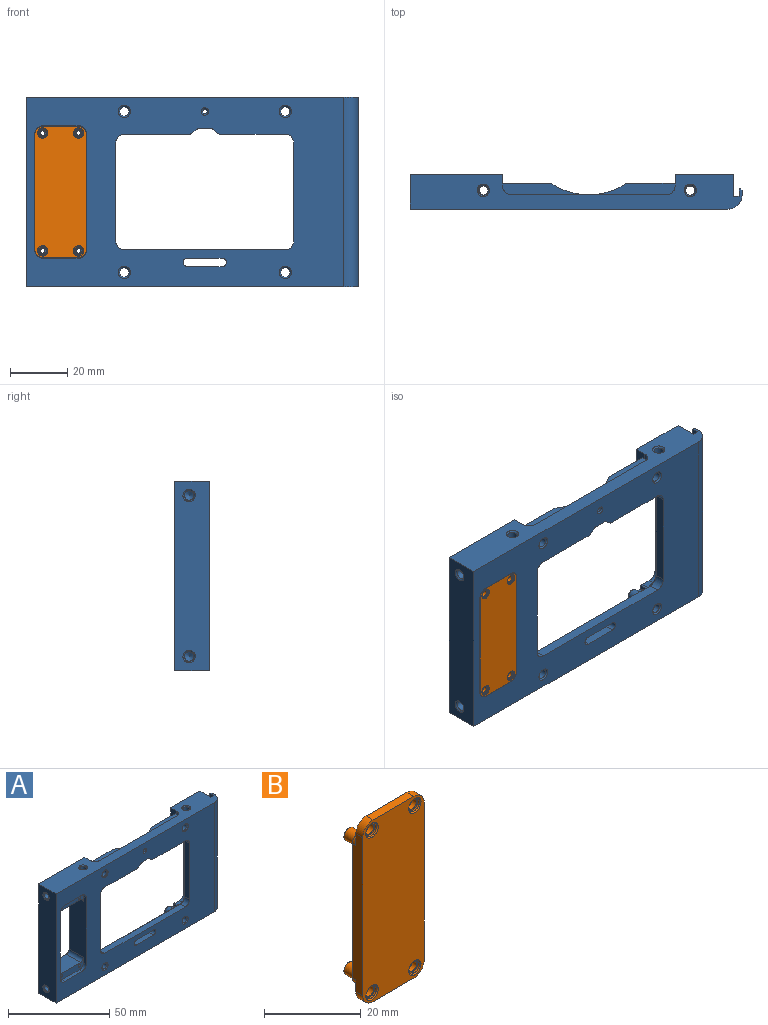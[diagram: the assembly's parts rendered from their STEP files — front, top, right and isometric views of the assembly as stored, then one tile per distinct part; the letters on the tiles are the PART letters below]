
ASSEMBLY  parts=2 mates=1
PART A: 193 faces, bbox 115.5x12x66 mm
  f0: plane 110.5x66mm, normal (0,-1,0), area 3867.2mm2, adj f15,f33,f34,f35,f36,f37,f38,f39
  f1: cylinder r=2mm len=10mm, axis (0,1,0), area 31.4mm2, adj f2,f31,f121,f173
  f2: plane 14.1x10mm, normal (0,0,-1), area 141mm2, adj f1,f3,f31,f173
  f3: cylinder r=2mm len=10mm, axis (0,1,0), area 31.4mm2, adj f2,f31,f122,f173
  f4: cylinder r=2mm len=10mm, axis (0,1,0), area 31.4mm2, adj f5,f31,f122,f177
  f5: plane 14.1x10mm, normal (0,0,1), area 141mm2, adj f4,f6,f31,f177
  f6: cylinder r=2mm len=10mm, axis (0,1,0), area 31.4mm2, adj f5,f31,f121,f177
  f7: cylinder r=0.8mm len=10mm, axis (0,-1,0), area 50.3mm2, adj f31,f173
  f8: cylinder r=0.8mm len=10mm, axis (0,-1,0), area 50.3mm2, adj f31,f177
  f9: cylinder r=0.8mm len=10mm, axis (0,-1,0), area 50.3mm2, adj f31,f177
  f10: cylinder r=0.8mm len=10mm, axis (0,-1,0), area 50.3mm2, adj f31,f173
  f11: plane 4.5x4.26mm, normal (1,0,0), area 19.2mm2, adj f15,f21,f139,f148
  f12: plane 4.5x4.26mm, normal (-1,0,0), area 19.2mm2, adj f15,f21,f140,f149
  f13: cylinder r=3.5mm len=4.5mm, axis (0,-1,0), area 6.6mm2, adj f21,f113,f139,f147
  f14: cylinder r=3.5mm len=4.5mm, axis (0,-1,0), area 6.6mm2, adj f18,f21,f140,f150
  f15: plane 115.5x12mm, normal (0,0,-1), area 923.5mm2, adj f0,f11,f12,f21,f24,f31,f54,f56
  f16: cylinder r=1.65mm len=8.5mm, axis (0,1,0), area 88.1mm2, adj f123,f140
  f17: cylinder r=1.65mm len=8.5mm, axis (0,1,0), area 88.1mm2, adj f126,f139
  f18: cylinder r=5mm len=7.5mm, axis (0,-1,0), area 16mm2, adj f14,f21,f24,f90,f119,f140
  f19: cylinder r=2mm len=4.5mm, axis (0,-1,0), area 26.3mm2, adj f21,f140,f149,f150
  f20: cylinder r=2mm len=4.5mm, axis (0,-1,0), area 26.3mm2, adj f21,f139,f147,f148
  f21: plane 78x56.5mm, normal (0,1,0), area 1353.3mm2, adj f11,f12,f13,f14,f15,f18,f19,f20
  f22: plane 8.11x7.5mm, normal (0,0,-1), area 48mm2, adj f21,f24,f49,f94,f116,f128,f138
  f23: plane 8.11x7.5mm, normal (0,0,-1), area 52.5mm2, adj f21,f31,f69,f93,f117,f127,f135
  f24: plane 66x20.3mm, normal (0,1,0), area 508.5mm2, adj f15,f18,f22,f55,f59,f86,f87,f90
  f25: cylinder r=24mm len=26.53mm, axis (0,0,1), area 208.8mm2, adj f28,f29,f30,f57,f127,f128
  f26: cylinder r=1.65mm len=8.5mm, axis (0,1,0), area 88.1mm2, adj f125,f127
  f27: cylinder r=1.65mm len=8.5mm, axis (0,1,0), area 88.1mm2, adj f124,f128
  f28: plane 43.29x4.5mm, normal (0,0,-1), area 122.8mm2, adj f21,f25,f127,f128,f136,f137
  f29: plane 30x4mm, normal (0,0,1), area 82.1mm2, adj f25,f114,f115,f116,f128
  f30: plane 30x4mm, normal (0,0,1), area 82.1mm2, adj f25,f114,f117,f118,f127
  f31: plane 66x32.2mm, normal (0,1,0), area 956.1mm2, adj f1,f2,f3,f4,f5,f6,f7,f8
  f32: plane 7.5x3.18mm, normal (0,0,1), area 21.8mm2, adj f21,f31,f64,f91,f113
  f33: plane 56.05x3.5mm, normal (0,0,1), area 196.2mm2, adj f0,f46,f47,f105
  f34: cylinder r=3mm len=3.5mm, axis (0,1,0), area 16.5mm2, adj f0,f35,f48,f111
  f35: plane 22.53x3.5mm, normal (0,0,-1), area 78.8mm2, adj f0,f34,f36,f112
  f36: cylinder r=1.45mm len=3.5mm, axis (0,1,0), area 3.5mm2, adj f0,f35,f37,f110
  f37: plane 3.5x1.59mm, normal (0.64,0,-0.77), area 7.3mm2, adj f0,f36,f38,f108
  f38: cylinder r=1.53mm len=3.5mm, axis (0,1,0), area 3.7mm2, adj f0,f37,f39,f106
  f39: plane 4x3.5mm, normal (0,0,-1), area 14mm2, adj f0,f38,f40,f104
  f40: cylinder r=1.53mm len=3.5mm, axis (0,1,0), area 3.7mm2, adj f0,f39,f41,f102
  f41: plane 3.5x1.59mm, normal (-0.64,0,-0.77), area 7.3mm2, adj f0,f40,f42,f100
  f42: cylinder r=1.45mm len=3.5mm, axis (0,1,0), area 3.5mm2, adj f0,f41,f43,f98
  f43: plane 22.53x3.5mm, normal (0,0,-1), area 78.8mm2, adj f0,f42,f44,f97
  f44: cylinder r=3mm len=3.5mm, axis (0,1,0), area 16.5mm2, adj f0,f43,f45,f99
  f45: plane 34.05x3.5mm, normal (-1,0,0), area 119.2mm2, adj f0,f44,f46,f101
  f46: cylinder r=3mm len=3.5mm, axis (0,1,0), area 16.5mm2, adj f0,f33,f45,f103
  f47: cylinder r=3mm len=3.5mm, axis (0,1,0), area 16.5mm2, adj f0,f33,f48,f107
  f48: plane 34.05x3.5mm, normal (1,0,0), area 119.2mm2, adj f0,f34,f47,f109
  f49: cylinder r=1.65mm len=9.15mm, axis (0,0,1), area 93.6mm2, adj f22,f71,f94
  f50: cylinder r=1.5mm len=4.5mm, axis (0,1,0), area 21.2mm2, adj f0,f21,f51,f53
  f51: plane 12x4.5mm, normal (0,0,-1), area 54mm2, adj f0,f21,f50,f52
  f52: cylinder r=1.5mm len=4.5mm, axis (0,1,0), area 21.2mm2, adj f0,f21,f51,f53
  f53: plane 12x4.5mm, normal (0,0,1), area 54mm2, adj f0,f21,f50,f52
  f54: plane 66x1.5mm, normal (1,0,0), area 99mm2, adj f15,f55,f58,f63
  f55: plane 115.5x12mm, normal (0,0,1), area 915.3mm2, adj f0,f24,f31,f54,f56,f58,f59,f60
  f56: plane 66x12mm, normal (-1,0,0), area 763mm2, adj f0,f15,f31,f55,f76,f77
  f57: cylinder r=0.8mm len=4.5mm, axis (0,1,0), area 22.6mm2, adj f25,f169
  f58: cylinder r=5mm len=66mm, axis (0,0,-1), area 518.4mm2, adj f0,f15,f54,f55
  f59: plane 66x7.5mm, normal (1,0,0), area 495mm2, adj f15,f24,f55,f60
  f60: plane 66x2mm, normal (0,1,0), area 132mm2, adj f15,f55,f59,f61
  f61: plane 66x2.5mm, normal (-1,0,0), area 165mm2, adj f15,f55,f60,f62
  f62: plane 66x0.5mm, normal (0,1,0), area 33mm2, adj f15,f55,f61,f63
  f63: plane 66x0.5mm, normal (0.71,0.71,0), area 46.7mm2, adj f15,f54,f55,f62
  f64: cylinder r=1.65mm len=7.64mm, axis (0,0,-1), area 70.8mm2, adj f32,f67,f91
  f65: cylinder r=1.65mm len=6.65mm, axis (0,0,-1), area 67.7mm2, adj f66,f90,f96
  f66: cone r=1.65mm half-angle=45deg, axis (0,0,-1), area 8.4mm2, adj f15,f65
  f67: cone r=1.65mm half-angle=45deg, axis (0,0,-1), area 8.4mm2, adj f15,f64
  f68: cone r=0mm half-angle=59deg, axis (0,0,1), area 0.9mm2, adj f69,f93
  f69: cylinder r=1.65mm len=9.5mm, axis (0,0,1), area 95.5mm2, adj f23,f68,f70,f93
  f70: cone r=1.65mm half-angle=45deg, axis (0,0,1), area 8.4mm2, adj f55,f69
  f71: cone r=1.65mm half-angle=45deg, axis (0,0,1), area 8.4mm2, adj f49,f55
  f72: cone r=0mm half-angle=59deg, axis (-1,0,0), area 10mm2, adj f73
  f73: cylinder r=1.65mm len=11.6mm, axis (-1,0,0), area 120.3mm2, adj f72,f77
  f74: cone r=0mm half-angle=59deg, axis (-1,0,0), area 10mm2, adj f75
  f75: cylinder r=1.65mm len=11.6mm, axis (-1,0,0), area 120.3mm2, adj f74,f76
  f76: cone r=1.65mm half-angle=45deg, axis (-1,0,0), area 8.4mm2, adj f56,f75
  f77: cone r=1.65mm half-angle=45deg, axis (-1,0,0), area 8.4mm2, adj f56,f73
  f78: cone r=0mm half-angle=59deg, axis (0,1,0), area 5.7mm2, adj f79
  f79: cylinder r=1.25mm len=8mm, axis (0,1,0), area 62.8mm2, adj f78,f89
  f80: cone r=0mm half-angle=59deg, axis (0,1,0), area 5.7mm2, adj f81
  f81: cylinder r=1.25mm len=8mm, axis (0,1,0), area 62.8mm2, adj f80,f88
  f82: cone r=0mm half-angle=59deg, axis (0,1,0), area 5.7mm2, adj f83
  f83: cylinder r=1.25mm len=8mm, axis (0,1,0), area 62.8mm2, adj f82,f87
  f84: cone r=0mm half-angle=59deg, axis (0,1,0), area 5.7mm2, adj f85
  f85: cylinder r=1.25mm len=8mm, axis (0,1,0), area 62.8mm2, adj f84,f86
  f86: cone r=1.25mm half-angle=45deg, axis (0,1,0), area 6.7mm2, adj f24,f85
  f87: cone r=1.25mm half-angle=45deg, axis (0,1,0), area 6.7mm2, adj f24,f83
  f88: cone r=1.25mm half-angle=45deg, axis (0,1,0), area 6.7mm2, adj f31,f81
  f89: cone r=1.25mm half-angle=45deg, axis (0,1,0), area 6.7mm2, adj f31,f79
  f90: plane 7.5x3.18mm, normal (0,0,1), area 17.3mm2, adj f18,f21,f24,f65,f96
  f91: cylinder r=3mm len=7.5mm, axis (0,1,0), area 28.1mm2, adj f21,f31,f32,f64,f92
  f92: plane 43.5x7.5mm, normal (1,0,0), area 326.2mm2, adj f21,f31,f91,f93
  f93: cylinder r=3mm len=7.5mm, axis (0,1,0), area 29.1mm2, adj f21,f23,f31,f68,f69,f92
  f94: cylinder r=3mm len=7.5mm, axis (0,1,0), area 33.3mm2, adj f21,f22,f24,f49,f95
  f95: plane 43.5x7.5mm, normal (-1,0,0), area 326.2mm2, adj f21,f24,f94,f96
  f96: cylinder r=3mm len=7.5mm, axis (0,1,0), area 33.3mm2, adj f21,f24,f65,f90,f95
  f97: plane 22.53x1mm, normal (0,0.71,-0.71), area 31.9mm2, adj f21,f43,f98,f99
  f98: cone r=0.45mm half-angle=45deg, axis (0,-1,0), area 0.9mm2, adj f21,f42,f97,f100
  f99: cone r=3mm half-angle=45deg, axis (0,1,0), area 7.8mm2, adj f21,f44,f97,f101
  f100: plane 2.23x2.1mm, normal (-0.45,0.71,-0.54), area 2.9mm2, adj f21,f41,f98,f102
  f101: plane 34.05x1mm, normal (-0.71,0.71,0), area 48.2mm2, adj f21,f45,f99,f103
  f102: cone r=1.53mm half-angle=45deg, axis (0,1,0), area 2mm2, adj f21,f40,f100,f104
  f103: cone r=3mm half-angle=45deg, axis (0,1,0), area 7.8mm2, adj f21,f46,f101,f105
  f104: plane 4x1mm, normal (0,0.71,-0.71), area 5.7mm2, adj f21,f39,f102,f106
  f105: plane 56.05x1mm, normal (0,0.71,0.71), area 79.3mm2, adj f21,f33,f103,f107
  f106: cone r=2.52mm half-angle=45deg, axis (0,1,0), area 2mm2, adj f21,f38,f104,f108
  f107: cone r=3mm half-angle=45deg, axis (0,1,0), area 7.8mm2, adj f21,f47,f105,f109
  f108: plane 2.23x2.1mm, normal (0.45,0.71,-0.54), area 2.9mm2, adj f21,f37,f106,f110
  f109: plane 34.05x1mm, normal (0.71,0.71,0), area 48.2mm2, adj f21,f48,f107,f111
  f110: cone r=1.45mm half-angle=45deg, axis (0,-1,0), area 0.9mm2, adj f21,f36,f108,f112
  f111: cone r=3mm half-angle=45deg, axis (0,1,0), area 7.8mm2, adj f21,f34,f109,f112
  f112: plane 22.53x1mm, normal (0,0.71,-0.71), area 31.9mm2, adj f21,f35,f110,f111
  f113: cylinder r=5mm len=7.5mm, axis (0,-1,0), area 16mm2, adj f13,f21,f31,f32,f120,f139
  f114: plane 54x2mm, normal (0,1,0), area 108mm2, adj f29,f30,f55,f115,f118
  f115: cylinder r=3mm len=3mm, axis (0,0,1), area 9.4mm2, adj f29,f55,f114,f116
  f116: plane 9.5x4mm, normal (-1,0,0), area 30.5mm2, adj f22,f24,f29,f55,f115,f128
  f117: plane 9.5x4mm, normal (1,0,0), area 30.5mm2, adj f23,f30,f31,f55,f118,f127
  f118: cylinder r=3mm len=3mm, axis (0,0,1), area 9.4mm2, adj f30,f55,f114,f117
  f119: plane 7.07x3mm, normal (-1,0,0), area 21.2mm2, adj f15,f18,f24,f140
  f120: plane 7.07x3mm, normal (1,0,0), area 21.2mm2, adj f15,f31,f113,f139
  f121: plane 40.1x12mm, normal (1,0,0), area 421.2mm2, adj f0,f1,f6,f31,f170,f173,f174,f177
  f122: plane 40.1x12mm, normal (-1,0,0), area 421.2mm2, adj f0,f3,f4,f31,f171,f173,f176,f177
  f123: cone r=1.65mm half-angle=45deg, axis (0,-1,0), area 8.4mm2, adj f0,f16
  f124: cone r=2.15mm half-angle=45deg, axis (0,-1,0), area 8.4mm2, adj f0,f27
  f125: cone r=1.65mm half-angle=45deg, axis (0,-1,0), area 8.4mm2, adj f0,f26
  f126: cone r=2.15mm half-angle=45deg, axis (0,-1,0), area 8.4mm2, adj f0,f17
  f127: plane 16.73x8.24mm, normal (0,1,0), area 114mm2, adj f23,f25,f26,f28,f30,f117,f132,f133
  f128: plane 16.73x8.24mm, normal (0,1,0), area 114mm2, adj f22,f25,f27,f28,f29,f116,f130,f134
  f129: cone r=0mm half-angle=59deg, axis (0,1,0), area 5.7mm2, adj f130
  f130: cylinder r=1.25mm len=5.5mm, axis (0,1,0), area 43.2mm2, adj f128,f129
  f131: cone r=0mm half-angle=59deg, axis (0,1,0), area 5.7mm2, adj f132
  f132: cylinder r=1.25mm len=5.5mm, axis (0,1,0), area 43.2mm2, adj f127,f131
  f133: cylinder r=2mm len=4.5mm, axis (0,1,0), area 8.3mm2, adj f21,f127,f135,f136
  f134: cylinder r=2mm len=4.5mm, axis (0,1,0), area 8.3mm2, adj f21,f128,f137,f138
  f135: cylinder r=5mm len=4.5mm, axis (0,1,0), area 10.4mm2, adj f21,f23,f127,f133
  f136: cylinder r=5mm len=4.5mm, axis (0,1,0), area 10.4mm2, adj f21,f28,f127,f133
  f137: cylinder r=5mm len=4.5mm, axis (0,1,0), area 10.4mm2, adj f21,f28,f128,f134
  f138: cylinder r=5mm len=4.5mm, axis (0,1,0), area 10.4mm2, adj f21,f22,f128,f134
  f139: plane 10.24x9.24mm, normal (0,1,0), area 55.4mm2, adj f11,f13,f15,f17,f20,f113,f120,f145
  f140: plane 10.24x9.24mm, normal (0,1,0), area 55.4mm2, adj f12,f14,f15,f16,f18,f19,f119,f146
  f141: cone r=0mm half-angle=59deg, axis (0,1,0), area 5.7mm2, adj f142
  f142: cylinder r=1.25mm len=5mm, axis (0,1,0), area 39.3mm2, adj f141,f145
  f143: cone r=0mm half-angle=59deg, axis (0,1,0), area 5.7mm2, adj f144
  f144: cylinder r=1.25mm len=5mm, axis (0,1,0), area 39.3mm2, adj f143,f146
  f145: cone r=1.25mm half-angle=45deg, axis (0,1,0), area 6.7mm2, adj f139,f142
  f146: cone r=1.25mm half-angle=45deg, axis (0,1,0), area 6.7mm2, adj f140,f144
  f147: cylinder r=5mm len=4.5mm, axis (0,1,0), area 12.8mm2, adj f13,f20,f21,f139
  f148: cylinder r=5mm len=4.5mm, axis (0,-1,0), area 13.6mm2, adj f11,f20,f21,f139
  f149: cylinder r=5mm len=4.5mm, axis (0,-1,0), area 13.6mm2, adj f12,f19,f21,f140
  f150: cylinder r=5mm len=4.5mm, axis (0,1,0), area 12.8mm2, adj f14,f19,f21,f140
  f151: cone r=0mm half-angle=59deg, axis (0,1,0), area 5.7mm2, adj f152
  f152: cylinder r=1.25mm len=2.5mm, axis (0,1,0), area 19.6mm2, adj f151,f168
  f153: cone r=0mm half-angle=59deg, axis (0,1,0), area 5.7mm2, adj f154
  f154: cylinder r=1.25mm len=2.5mm, axis (0,1,0), area 19.6mm2, adj f153,f163
  f155: cone r=0mm half-angle=59deg, axis (0,1,0), area 5.7mm2, adj f156
  f156: cylinder r=1.25mm len=2.5mm, axis (0,1,0), area 19.6mm2, adj f155,f164
  f157: cone r=0mm half-angle=59deg, axis (0,1,0), area 5.7mm2, adj f158
  f158: cylinder r=1.25mm len=2.5mm, axis (0,1,0), area 19.6mm2, adj f157,f165
  f159: cone r=0mm half-angle=59deg, axis (0,1,0), area 5.7mm2, adj f160
  f160: cylinder r=1.25mm len=2.5mm, axis (0,1,0), area 19.6mm2, adj f159,f166
  f161: cone r=0mm half-angle=59deg, axis (0,1,0), area 5.7mm2, adj f162
  f162: cylinder r=1.25mm len=2.5mm, axis (0,1,0), area 19.6mm2, adj f161,f167
  f163: cone r=1.25mm half-angle=45deg, axis (0,1,0), area 6.7mm2, adj f21,f154
  f164: cone r=1.25mm half-angle=45deg, axis (0,1,0), area 6.7mm2, adj f21,f156
  f165: cone r=1.25mm half-angle=45deg, axis (0,1,0), area 6.7mm2, adj f21,f158
  f166: cone r=1.25mm half-angle=45deg, axis (0,1,0), area 6.7mm2, adj f21,f160
  f167: cone r=1.25mm half-angle=45deg, axis (0,1,0), area 6.7mm2, adj f21,f162
  f168: cone r=1.25mm half-angle=45deg, axis (0,1,0), area 6.7mm2, adj f21,f152
  f169: cone r=0.8mm half-angle=45deg, axis (0,-1,0), area 4.7mm2, adj f0,f57
  f170: cylinder r=3mm len=3mm, axis (0,-1,0), area 9.4mm2, adj f0,f121,f172,f173
  f171: cylinder r=3mm len=3mm, axis (0,-1,0), area 9.4mm2, adj f0,f122,f172,f173
  f172: plane 12.1x2mm, normal (0,0,-1), area 24.2mm2, adj f0,f170,f171,f173
  f173: plane 18.1x6mm, normal (0,-1,0), area 66.2mm2, adj f1,f2,f3,f7,f10,f121,f122,f170
  f174: cylinder r=3mm len=3mm, axis (0,-1,0), area 9.4mm2, adj f0,f121,f175,f177
  f175: plane 12.1x2mm, normal (0,0,1), area 24.2mm2, adj f0,f174,f176,f177
  f176: cylinder r=3mm len=3mm, axis (0,-1,0), area 9.4mm2, adj f0,f122,f175,f177
  f177: plane 18.1x6mm, normal (0,-1,0), area 66.2mm2, adj f4,f5,f6,f8,f9,f121,f122,f174
  f178: plane 10x0.24mm, normal (0,0,-1), area 2.4mm2, adj f24,f179,f189,f190
  f179: cylinder r=1mm len=10mm, axis (0,1,0), area 15.7mm2, adj f24,f178,f180,f190
  f180: plane 10x5mm, normal (-1,0,0), area 50mm2, adj f24,f179,f190,f191
  f181: cylinder r=1.5mm len=10mm, axis (0,1,0), area 22.4mm2, adj f24,f182,f190,f191
  f182: plane 39.03x10mm, normal (-1,0,0), area 390.3mm2, adj f24,f181,f183,f190
  f183: cylinder r=1.5mm len=10mm, axis (0,1,0), area 22.4mm2, adj f24,f182,f190,f192
  f184: plane 10x5mm, normal (-1,0,0), area 50mm2, adj f24,f185,f190,f192
  f185: cylinder r=1mm len=10mm, axis (0,1,0), area 15.7mm2, adj f24,f184,f186,f190
  f186: plane 10x0.24mm, normal (0,0,1), area 2.4mm2, adj f24,f185,f187,f190
  f187: cylinder r=1mm len=10mm, axis (0,1,0), area 15.7mm2, adj f24,f186,f188,f190
  f188: plane 60x10mm, normal (1,0,0), area 600mm2, adj f24,f187,f189,f190
  f189: cylinder r=1mm len=10mm, axis (0,1,0), area 15.7mm2, adj f24,f178,f188,f190
  f190: plane 62x7.3mm, normal (0,1,0), area 356.5mm2, adj f178,f179,f180,f181,f182,f183,f184,f185
  f191: cylinder r=4mm len=10mm, axis (0,1,0), area 59.6mm2, adj f24,f180,f181,f190
  f192: cylinder r=4mm len=10mm, axis (0,1,0), area 59.6mm2, adj f24,f183,f184,f190
PART B: 50 faces, bbox 17.9x6x45.9 mm
  f0: cylinder r=1.2mm len=2.4mm, axis (0,1,0), area 9.8mm2, adj f14,f39
  f1: cylinder r=1.2mm len=2.4mm, axis (0,1,0), area 9.8mm2, adj f4,f45
  f2: cylinder r=1.2mm len=2.4mm, axis (0,1,0), area 9.8mm2, adj f4,f43
  f3: cylinder r=1.2mm len=2.4mm, axis (0,1,0), area 9.8mm2, adj f14,f41
  f4: plane 17.9x5.99mm, normal (0,1,0), area 60.1mm2, adj f1,f2,f5,f9,f10,f11,f12,f17
  f5: plane 39.9x3mm, normal (1,0,0), area 113.7mm2, adj f4,f6,f12,f13,f14,f16,f17,f21
  f6: cylinder r=3mm len=3mm, axis (0,1,0), area 9.4mm2, adj f5,f7,f13,f14
  f7: plane 11.9x2mm, normal (0,0,1), area 23.8mm2, adj f6,f8,f13,f14
  f8: cylinder r=3mm len=3mm, axis (0,1,0), area 9.4mm2, adj f7,f9,f13,f14
  f9: plane 39.9x3mm, normal (-1,0,0), area 113.7mm2, adj f4,f8,f10,f13,f14,f19,f20,f21
  f10: cylinder r=3mm len=3mm, axis (0,1,0), area 9.4mm2, adj f4,f9,f11,f13
  f11: plane 11.9x2mm, normal (0,0,-1), area 23.8mm2, adj f4,f10,f12,f13
  f12: cylinder r=3mm len=3mm, axis (0,1,0), area 9.4mm2, adj f4,f5,f11,f13
  f13: plane 45.9x17.9mm, normal (0,-1,0), area 773.2mm2, adj f5,f6,f7,f8,f9,f10,f11,f12
  f14: plane 17.9x5.99mm, normal (0,1,0), area 60.1mm2, adj f0,f3,f5,f6,f7,f8,f9,f15
  f15: plane 13.9x1mm, normal (0,0,1), area 13.9mm2, adj f14,f16,f20,f21
  f16: cylinder r=2mm len=2mm, axis (0,-1,0), area 3.1mm2, adj f5,f14,f15,f21
  f17: cylinder r=2mm len=2mm, axis (0,-1,0), area 3.1mm2, adj f4,f5,f18,f21
  f18: plane 13.9x1mm, normal (0,0,-1), area 13.9mm2, adj f4,f17,f19,f21
  f19: cylinder r=2mm len=2mm, axis (0,-1,0), area 3.1mm2, adj f4,f9,f18,f21
  f20: cylinder r=2mm len=2mm, axis (0,-1,0), area 3.1mm2, adj f9,f14,f15,f21
  f21: plane 37.93x17.9mm, normal (0,1,0), area 647.2mm2, adj f5,f9,f15,f16,f17,f18,f19,f20
  f22: cylinder r=1.5mm len=3mm, axis (0,-1,0), area 28.3mm2, adj f21,f23
  f23: plane 3x3mm, normal (0,1,0), area 5.1mm2, adj f22,f37
  f24: cylinder r=1.5mm len=3mm, axis (0,-1,0), area 28.3mm2, adj f21,f25
  f25: plane 3x3mm, normal (0,1,0), area 5.1mm2, adj f24,f35
  f26: cylinder r=1.5mm len=3mm, axis (0,-1,0), area 28.3mm2, adj f21,f27
  f27: plane 3x3mm, normal (0,1,0), area 5.1mm2, adj f26,f33
  f28: cylinder r=1.5mm len=3mm, axis (0,-1,0), area 28.3mm2, adj f21,f29
  f29: plane 3x3mm, normal (0,1,0), area 5.1mm2, adj f28,f31
  f30: cone r=0mm half-angle=59deg, axis (0,1,0), area 2.3mm2, adj f31
  f31: cylinder r=0.8mm len=4.2mm, axis (0,1,0), area 21.1mm2, adj f29,f30
  f32: cone r=0mm half-angle=59deg, axis (0,1,0), area 2.3mm2, adj f33
  f33: cylinder r=0.8mm len=4.2mm, axis (0,1,0), area 21.1mm2, adj f27,f32
  f34: cone r=0mm half-angle=59deg, axis (0,1,0), area 2.3mm2, adj f35
  f35: cylinder r=0.8mm len=4.2mm, axis (0,1,0), area 21.1mm2, adj f25,f34
  f36: cone r=0mm half-angle=59deg, axis (0,1,0), area 2.3mm2, adj f37
  f37: cylinder r=0.8mm len=4.2mm, axis (0,1,0), area 21.1mm2, adj f23,f36
  f38: cylinder r=1.55mm len=3.1mm, axis (0,-1,0), area 4.4mm2, adj f39,f49
  f39: plane 3.1x3.1mm, normal (0,-1,0), area 3mm2, adj f0,f38
  f40: cylinder r=1.55mm len=3.1mm, axis (0,-1,0), area 4.4mm2, adj f41,f48
  f41: plane 3.1x3.1mm, normal (0,-1,0), area 3mm2, adj f3,f40
  f42: cylinder r=1.55mm len=3.1mm, axis (0,-1,0), area 4.4mm2, adj f43,f47
  f43: plane 3.1x3.1mm, normal (0,-1,0), area 3mm2, adj f2,f42
  f44: cylinder r=1.55mm len=3.1mm, axis (0,-1,0), area 4.4mm2, adj f45,f46
  f45: plane 3.1x3.1mm, normal (0,-1,0), area 3mm2, adj f1,f44
  f46: cone r=1.55mm half-angle=45deg, axis (0,-1,0), area 3.7mm2, adj f13,f44
  f47: cone r=1.55mm half-angle=45deg, axis (0,-1,0), area 3.7mm2, adj f13,f42
  f48: cone r=1.55mm half-angle=45deg, axis (0,-1,0), area 3.7mm2, adj f13,f40
  f49: cone r=1.55mm half-angle=45deg, axis (0,-1,0), area 3.7mm2, adj f13,f38
PLACE A t=(17.27,-23.06,-25.32)mm
PLACE B t=(-23.93,-33.06,-48.27)mm
MATE fastened A.f7 <-> B.f0  axis (0,-1,0) through (-39.13,-33.06,-4.82)mm
